# Revit family: Pressure independent control valve F_4006_HF_UHF
name_source: partatom
category: Rohrzubehör
revit_build: Autodesk Revit 2018 (Build: 20190510_1515(x64)
units: mm (PartAtom-declared; Revit-internal decimal feet)

## family parameters
Arbeitsebenenbasiert = Nein
Beim Laden mit Abzugskörper schneiden = Nein
Bemaßung runder Anschluss = Durchmesser verwenden
Gemeinsam genutzt = Nein
Immer vertikal = Ja
OmniClass-Nummer = 23.65.55.14
OmniClass-Titel = Valves for Liquid Services
Teiletyp = Unterbricht

## types (2) — shared parameters
Application = the Pressure Independent Balancing Control Valve (PIBCV) is used in all heating and cooling systems with circulation pumps.
the valve automatically maintains flow to the required part of the system at the set rate by measuring and immediately adjusting to any variation in pressure.
no additional measurements are necessary and the correct flow rate is achieved at all operating conditions.
the diaphragm responds to the pressure upstream and downstream of the regulating valve (via an internal impulse line).
the valve settings directly affect the volumetric flow through the valve.
it is thus possible to set the maximum flow rate based on the flow chart when the valve is fitted.
this allows for the balancing of heating circuits, cooling water systems, ceiling cooling and heating panels, air heaters, etc. without any need to first assess the pressure variations in the system.
the valve‘s principal application is as a control valve for terminal units.
Cones = CW617N-R320-S
D03 = 21 mm
D07 = 30 mm  [stored 0.0984252 ft]
D08 = 24 mm  [stored 0.0787402 ft]
D13 = 16 mm  [stored 0.0524934 ft]
D14 = 17 mm
D15 = 5 mm  [stored 0.0164042 ft]
D16 = 10 mm  [stored 0.0328084 ft]
D17 = 3 mm  [stored 0.00984252 ft]
D18 = 4 mm  [stored 0.0131234 ft]
Diaphragm material = EPDM
Diff. pressure across the restrictor = 20000.0 Pa
H04 = 5 mm  [stored 0.0164042 ft]
H05 = 3 mm  [stored 0.00984252 ft]
H08 = 21 mm
H16 = 3 mm  [stored 0.00984252 ft]
H17 = 5 mm  [stored 0.0164042 ft]
H18 = 4 mm  [stored 0.0131234 ft]
Hersteller = Herz-Armaturen GmbH
Impulse tube = WN1.4301
K00 = 24 mm  [stored 0.0787402 ft]
K01 = 4 mm  [stored 0.0131234 ft]
K02 = 5 mm  [stored 0.0164042 ft]
K03 = 14 mm  [stored 0.0459318 ft]
L01 = 3 mm  [stored 0.00984252 ft]
L03 = 10 mm  [stored 0.0328084 ft]
M00 = 27 mm
M01 = 9 mm  [stored 0.0295276 ft]
M02 = 6 mm  [stored 0.019685 ft]
M03 = 3 mm  [stored 0.00984252 ft]
M04 = 2 mm  [stored 0.00656168 ft]
M05 = 4 mm  [stored 0.0131234 ft]
Medium = water purity in accordance with the OENORM H 5195 and VDI 2035 standards.
ethylene and propylene glycol can be mixed to a ratio of 25 - 50 vol. [%].
Membrane = EPDM
R02 = 13 mm
R03 = 7 mm  [stored 0.0229659 ft]
R04 = 8 mm  [stored 0.0262467 ft]
R05 = 5 mm  [stored 0.0164042 ft]
R97 = 2 mm  [stored 0.00656168 ft]
R98 = 6 mm  [stored 0.019685 ft]
R99 = 14 mm  [stored 0.0459318 ft]
SCRNCODE = 05;04;02
SCRNSEQ = ARM;ARM_TYP="DURR";2
Seat material = WN1.4305
Steam = WN1.4305
Type of Connection = EN 1092-2
URL = www.herzvalves.com
Valve body material = EN-GJL-250
max. Operating pressure = 1600000.0 Pa
max. Operating temperature = 110 °C
min. Operating pressure = 400000.0 Pa
min. Operating temperature (antifreeze) = -20 °C
min. Operating temperature (pure water) = 2 °C

## per-type parameters (varying)
| type | HF | UHF |
| HF | Ja | Nein |
| UHF | Nein | Ja |

note: [stored X ft] marks values corroborated as IEEE doubles in the binary element streams (Revit-internal decimal feet)
